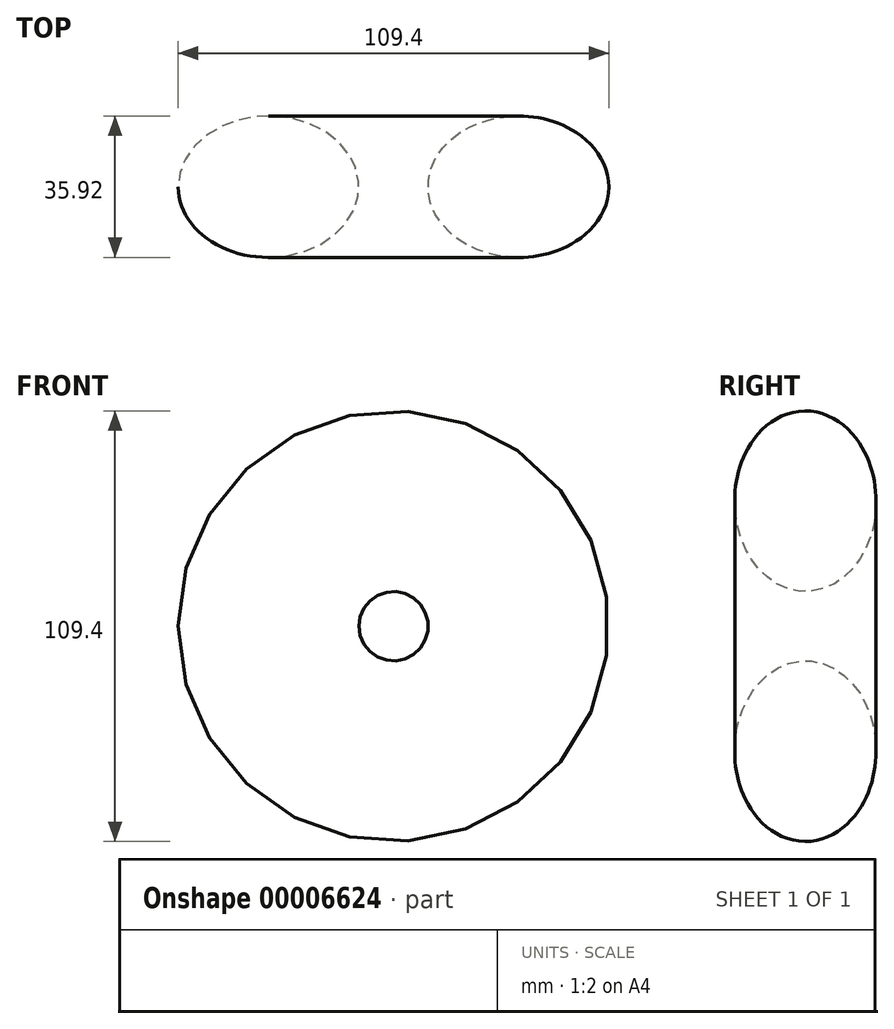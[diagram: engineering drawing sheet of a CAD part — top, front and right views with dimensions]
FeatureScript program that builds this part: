
annotation { "Feature Type Name" : "Feature", "Feature Type Description" : "" }
export const myFeature = defineFeature(function(context is Context, id is Id, definition is map)
    precondition{}
    {
        {
            var Q0;
            Q0=qCreatedBy(makeId("Top.planeOp"),FACE);
            var sketch = newSketch(context, id + "F0", { "sketchPlane" : qUnion([Q0])});
            skLineSegment(sketch, "E0", {"start": v(0, 0) * mm, "end": v(-31.75, 0) * mm, "construction": true});
            skEllipse(sketch, "E1", {"center": v(-31.75, 0) * mm, "majorRadius": 22.95 * mm, "minorRadius": 17.96 * mm, "majorAxis": v(-1, 0)});
            skLineSegment(sketch, "E2", {"start": v(0, 0) * mm, "end": v(0, 19.93) * mm, "construction": true});
            skSolve(sketch);
        }
        {
            var Q0;
            Q0 = qSketchRegion(id + "F0", true);
            var Q1;
            Q1=sQuery(id+"F0.wireOp",EDGE,"E2");
            revolve(context, id + "F1", {"entities" : qUnion([Q0]), "axis" : qUnion([Q1]), "revolveType" : RevolveType.FULL});
        }
    });
